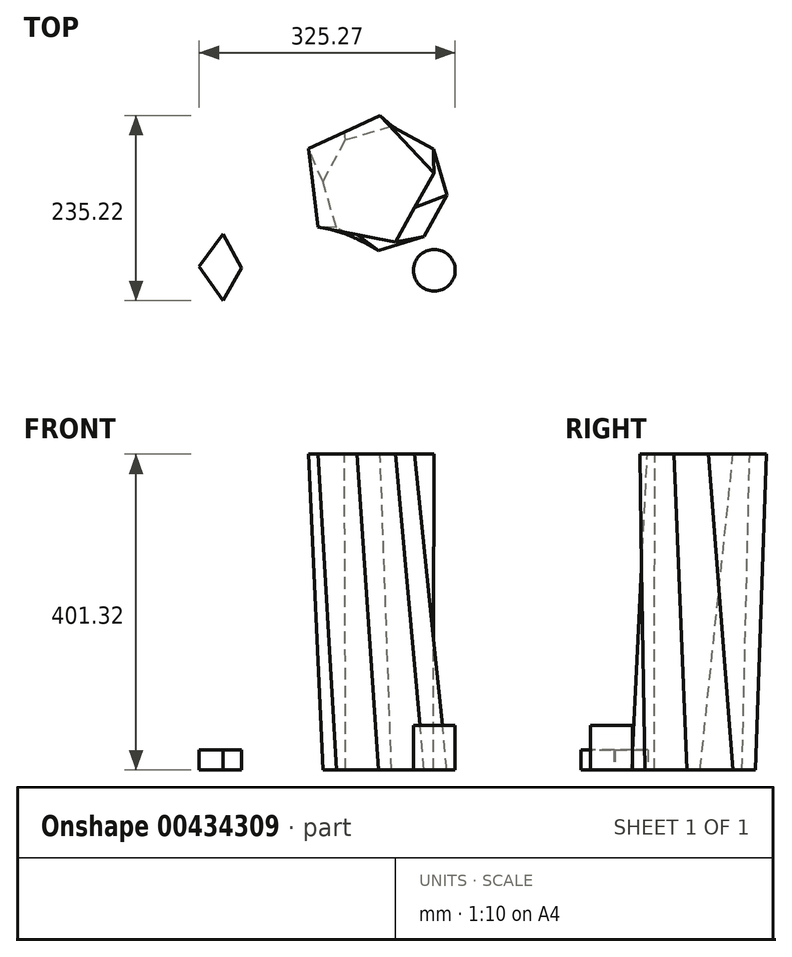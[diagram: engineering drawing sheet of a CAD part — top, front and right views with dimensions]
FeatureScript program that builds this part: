
annotation { "Feature Type Name" : "Feature", "Feature Type Description" : "" }
export const myFeature = defineFeature(function(context is Context, id is Id, definition is map)
    precondition{}
    {
        {
            var Q0;
            Q0=qCreatedBy(makeId("Top.planeOp"),FACE);
            var sketch = newSketch(context, id + "F0", { "sketchPlane" : qUnion([Q0])});
            skLineSegment(sketch, "E0", {"start": v(-173.83, -7.48) * mm, "end": v(-143.33, 33.96) * mm});
            skLineSegment(sketch, "E1", {"start": v(-143.33, 33.96) * mm, "end": v(-119.73, -9.2) * mm});
            skLineSegment(sketch, "E2", {"start": v(-119.73, -9.2) * mm, "end": v(-143.33, -50.65) * mm});
            skLineSegment(sketch, "E3", {"start": v(-143.33, -50.65) * mm, "end": v(-173.83, -7.48) * mm});
            skSolve(sketch);
        }
        {
            var Q0;
            Q0 = qSketchRegion(id + "F0", true);
            extrude(context, id + "F1", {"entities" : qUnion([Q0]), "depth" : 25.4 * mm});
        }
        {
            var Q0;
            Q0=qCreatedBy(makeId("Top.planeOp"),FACE);
            var sketch = newSketch(context, id + "F2", { "sketchPlane" : qUnion([Q0])});
            skCircle(sketch, "E4", {"center": v(124.9, -12.09) * mm, "radius": 26.53 * mm});
            skSolve(sketch);
        }
        {
            var Q0;
            Q0 = qSketchRegion(id + "F2", true);
            extrude(context, id + "F3", {"entities" : qUnion([Q0]), "depth" : 56.64 * mm});
        }
        {
            var Q0;
            Q0=qCreatedBy(makeId("Top.planeOp"),FACE);
            var sketch = newSketch(context, id + "F4", { "sketchPlane" : qUnion([Q0])});
            skCircle(sketch, "E5.cCircle", {"center": v(62.17, 92.1) * mm, "radius": 73.22 * mm, "construction": true});
            skLineSegment(sketch, "E5.0", {"start": v(111.98, 30.46) * mm, "end": v(53.8, 13.29) * mm});
            skLineSegment(sketch, "E5.1", {"start": v(53.8, 13.29) * mm, "end": v(0.52, 42.29) * mm});
            skLineSegment(sketch, "E5.2", {"start": v(0.52, 42.29) * mm, "end": v(-16.64, 100.46) * mm});
            skLineSegment(sketch, "E5.3", {"start": v(-16.64, 100.46) * mm, "end": v(12.36, 153.74) * mm});
            skLineSegment(sketch, "E5.4", {"start": v(12.36, 153.74) * mm, "end": v(70.53, 170.9) * mm});
            skLineSegment(sketch, "E5.5", {"start": v(70.53, 170.9) * mm, "end": v(123.8, 141.9) * mm});
            skLineSegment(sketch, "E5.6", {"start": v(123.8, 141.9) * mm, "end": v(140.97, 83.73) * mm});
            skLineSegment(sketch, "E5.7", {"start": v(140.97, 83.73) * mm, "end": v(111.98, 30.46) * mm});
            skPoint(sketch, "E5.0.midPoint", {"position": v(82.89, 21.87) * mm});
            skSolve(sketch);
        }
        {
            var Q0;
            Q0=makeQuery(id+"F4.imprint","IMPRINT",FACE,{"disambiguationData":[TD([[makeQuery(id+"F4.imprint","IMPRINT",EDGE,{"derivedFrom":sQuery(id+"F4.wireOp",EDGE,"E5.0")}),-1.0]])]});
            cPlane(context, id + "F5", {"entities" : qUnion([Q0]), "cplaneType" : CPlaneType.OFFSET, "offset" : 401.32 * mm, "width" : 152.4 * mm, "height" : 152.4 * mm});
        }
        {
            var Q0;
            Q0=qCreatedBy(id+"F5.planeOp",FACE);
            var sketch = newSketch(context, id + "F6", { "sketchPlane" : qUnion([Q0])});
            skCircle(sketch, "E6.cCircle", {"center": v(39.8, 101.03) * mm, "radius": 68.88 * mm, "construction": true});
            skLineSegment(sketch, "E6.0", {"start": v(124.34, 111.23) * mm, "end": v(75.63, 23.8) * mm});
            skLineSegment(sketch, "E6.1", {"start": v(75.63, 23.8) * mm, "end": v(-22.58, 43.09) * mm});
            skLineSegment(sketch, "E6.2", {"start": v(-22.58, 43.09) * mm, "end": v(-34.57, 142.46) * mm});
            skLineSegment(sketch, "E6.3", {"start": v(-34.57, 142.46) * mm, "end": v(56.22, 184.57) * mm});
            skLineSegment(sketch, "E6.4", {"start": v(56.22, 184.57) * mm, "end": v(124.34, 111.23) * mm});
            skPoint(sketch, "E6.0.midPoint", {"position": v(99.98, 67.51) * mm});
            skSolve(sketch);
        }
        {
            var Q0;
            Q0=makeQuery(id+"F4.imprint","IMPRINT",FACE,{"disambiguationData":[TD([[makeQuery(id+"F4.imprint","IMPRINT",EDGE,{"derivedFrom":sQuery(id+"F4.wireOp",EDGE,"E5.0")}),-1.0]])]});
            var Q1;
            Q1=makeQuery(id+"F6.imprint","IMPRINT",FACE,{"disambiguationData":[TD([[makeQuery(id+"F6.imprint","IMPRINT",EDGE,{"derivedFrom":sQuery(id+"F6.wireOp",EDGE,"E6.0")}),-1.0]])]});
            loft(context, id + "F7", {"sheetProfilesArray" : [{ "sheetProfileEntities" : qUnion([Q0]) }, { "sheetProfileEntities" : qUnion([Q1]) }]});
        }
    });
